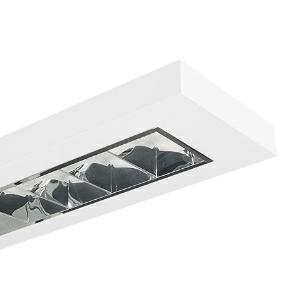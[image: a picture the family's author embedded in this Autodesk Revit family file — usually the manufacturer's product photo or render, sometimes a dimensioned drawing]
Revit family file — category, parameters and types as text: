
# Revit family: 3f_filippi_-_3f_travetta_di_2mg_3f_filippi_-_10748_-_3f_travetta_led_di_2x22w_2mg_l1590
name_source: partatom
category: Lighting Fixtures
units: mm (PartAtom-declared; Revit-internal decimal feet)

## family parameters
Cut with Voids When Loaded = No
Host = Face
Light Source = No
Part Type = Normal
Room Calculation Point = No
Round Connector Dimension = Use Diameter
Shared = No

## types (1)
- 3F Filippi - 3F Travetta DI 2MG (1 x LED, 5865 lm, 49 W, 4000 K)
    Apparent Load = 49 VA
    Approval mark = ENEC
    CIE Flux Codes = 61 98 100 85 100
    Color Rendering = 80
    Color Temperature = 4000 K
    Control Gear = Electronic ballast
    Default Elevation = 1800 mm
    Description = ILLUMINOTECHNICAL
Luminous efficiency 100% (DLOR 85%, ULOR 15%).
Initial luminous flux of the luminaire 5865 lm.
Symmetric direct-indirect distribution.
Installation Interdistance Transv.D = 2.02 x hu - Long.D = 1.27 x hu.
Average luminance <1000 cd/m² for radial angles >65°.
Tabular UGR (CIE 117 - 4H-8H; S=0.25H; 70/50/20): RUG 18.4 - 17.8.
Beam angle: 99° - 72°.
Luminous efficacy 120 lm/W.
Lifetime (L93/B10): 30000 h. (tq+25°C)
Lifetime (L90/B10): 50000 h. (tq+25°C)
Lifetime (L85/B10): 80000 h. (tq+25°C)
Lifetime (L80/B10): 100000 h. (tq+25°C)
Sudden decreased luminous flux after 50000 hours: 0% (C0).
Photobiological safety in compliance with IEC/TR 62778: RG0 risk exempt, (IEC 62471).
In compliance with IEC/EN 62722-2-1 - IEC/EN 62717 standards.

SOURCE
2 linear LED modules 22W/840.
Energy efficiency class (UE 2019/2020 - UE 2019/2015): D.
CIE 13.3 Colour rendering index: CRI >80 (R9 <50%).
IES TM-30 Fidelity Index: Rf = 84 Rg = 95.
CCT nominal colour temperature 4000 K.
Colour initial tolerance (MacAdam): SDCM 2.

MECHANICAL
Housing with squared shape in white painted galvannealed steel, with nonreflecting surface.
2MG parabolic louvre, high efficiency, in specular aluminium with superficial titanium-magnesium treatment, non-iridescent, with transverse blades closed at the top.
Prismatic flat diffuser in transparent methacrylate (PMMA), multilenticular, anti-glare, prismatic exterior, placed above louvre blades.
Film protective against dust and finger marks, adhesive, attached to louvre.
Upper holes closing film made of opal polycarbonate.
Luminaire with limited surface temperature. - D - (EN 60598-2-24)
Dimensions: 1590x190 mm, height 60 mm (edge 40 mm). Weight 4.96 kg.
IP20 protection degree.
Mechanical strength to impacts IK02 (0.2 joule).
Glow-wire test resistance 650°C.

ELECTRICAL
Halogen Free electronic wiring 230V-50/60Hz, power factor 0.95, THD <25%, constant output current, SELV, class I, 1 driver.
Power of the luminaire 49 W.
CE - IEC 60598-1 - EN 60598-1.
SAFE FLICKER: PstLM=<1 and SVM=<0.4 (IEC TR 61547-1 and IEC TR 63158), to ensure a more comfortable and safe light.
Luminaire compliant with EN 60598-2-22 for power supply from a centralised emergency system CPSS (Central Power Supply System), not incorporated in the luminaire - high risk areas excluded. The default power and flux are 100% in AC and 100% in DC.
Ambient temperature from 0°C to +25°C.
Temperature class T6 max 85°C.
Relative humidity UR: <85%.

INSTALLATION
Suspended.
All accessories dedicated to this product are available on the Catalog and on our website www.3F-Filippi.com.

APPLICATIONS
In environments, even with reduced height, requiring a comfortable light.
In environments with VDTs, managerial offices and staterooms, public offices and schools.

WARNING
Luminaire designed for disposal/recycling at end-of-life.
Replaceable (LED only) light source by a professional. Replaceable control gear by a professional.
    Height = 60 mm  [stored 0.19685 ft]
    Lamp = 1 x LED
    Lamp Light Flux = 5865 lm
    Lamp Power = 49 W
    Lamp count = 1
    Length = 1590 mm
    Lifetime = 50000 h
    Luminous efficacy = 120 lm/W
    Manufacturer = 3F Filippi
    ModVariant = No
    Model = 3F Filippi - 10748 - 3F Travetta LED DI 2x22W 2MG L1590
    Mounting Place = Ceiling
    Mounting Type = Pendant
    Number of Poles = 1
    OnlyDefault = Yes
    Power Factor = 1
    Product Name = 3F Filippi - 3F Travetta DI 2MG
    Product group = pendant luminaire
    ProductGroupID = 9
    Protection Class = Protection class I
    Protection Degree = IP 20
    RLX_Detail_Level = 1
    RLX_Emergency_Light_Flux = 0 lm
    RLX_Emergency_Type = 0
    RLX_Emergency_Type_DB = No
    RlxData = <blob elided: 51257 chars, md5=24582d3a>
    Socket = socket
    Standby Power = 0 W
    System Light Flux = 5865 lm
    System Power = 49 W
    Type Comments = Product without accessories
    Type Image = 3ffilippi_3f_travetta_led_2mg.jpg
    URL = http://relux.com
    VarID = ---
    Voltage = 0 V
    Weight = 0.00 kg
    Width = 190 mm  [stored 0.62336 ft]

note: [stored X ft] marks values corroborated as IEEE doubles in the binary element streams (Revit-internal decimal feet)

## geometry (parser evidence)
native form markers: Blend x4, Sweep x14
no freeform markers — native parametric forms only
